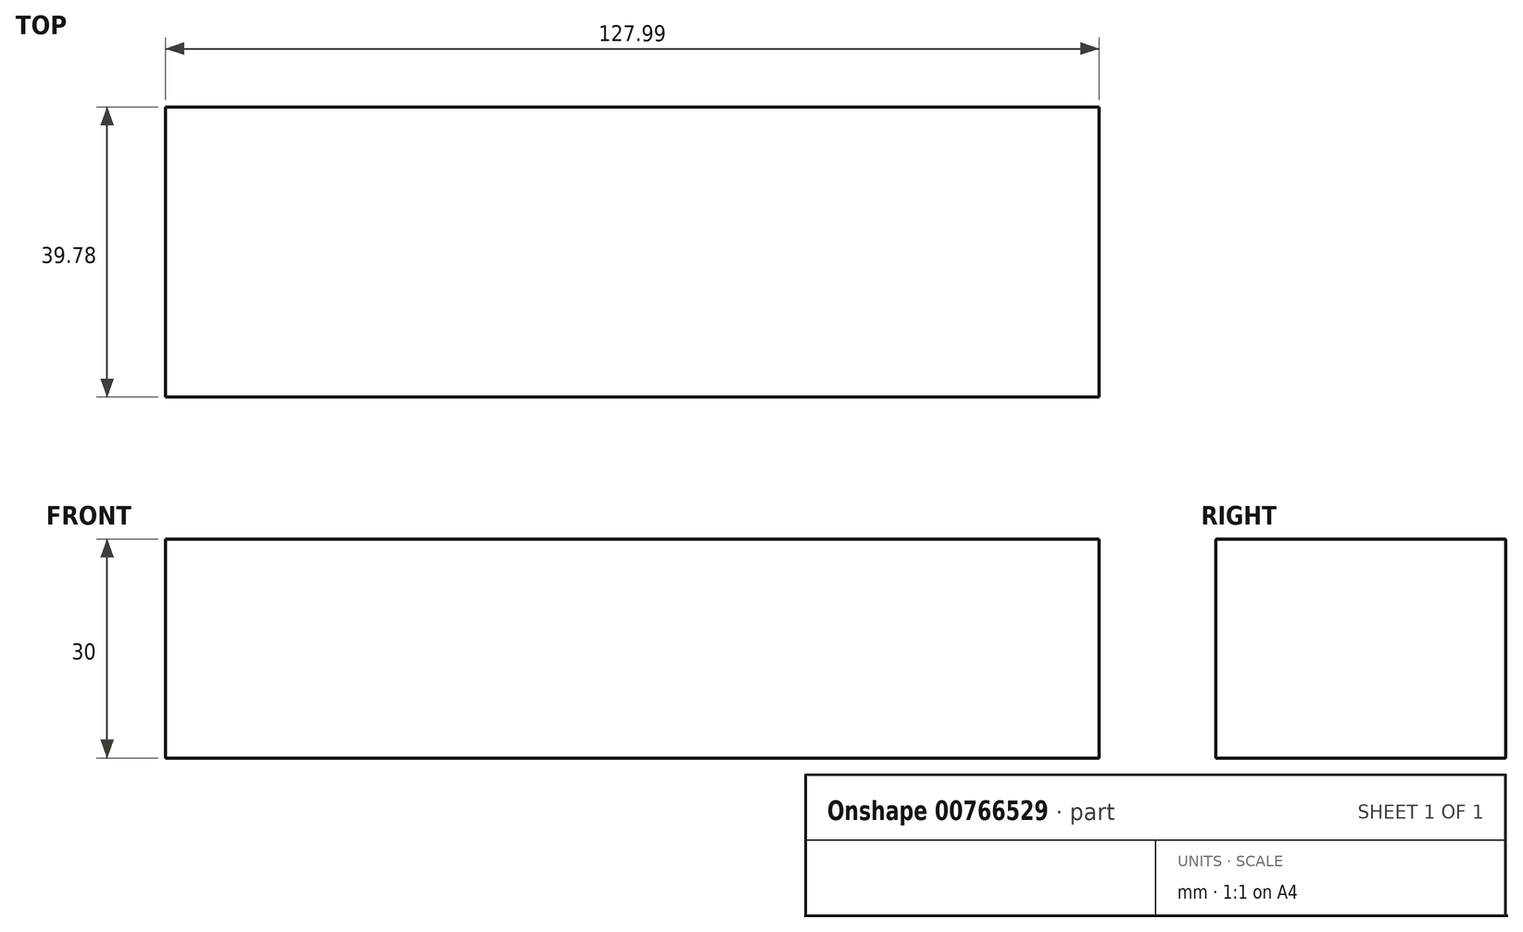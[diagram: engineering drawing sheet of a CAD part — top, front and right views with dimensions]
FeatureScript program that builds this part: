
annotation { "Feature Type Name" : "Feature", "Feature Type Description" : "" }
export const myFeature = defineFeature(function(context is Context, id is Id, definition is map)
    precondition{}
    {
        {
            var Q0;
            Q0=qCreatedBy(makeId("Top.planeOp"),FACE);
            var sketch = newSketch(context, id + "F0", { "sketchPlane" : qUnion([Q0])});
            skLineSegment(sketch, "E0.bottom", {"start": v(0, 0) * mm, "end": v(128, 0) * mm});
            skLineSegment(sketch, "E0.top", {"start": v(0, -39.78) * mm, "end": v(128, -39.78) * mm});
            skLineSegment(sketch, "E0.left", {"start": v(0, 0) * mm, "end": v(0, -39.78) * mm});
            skLineSegment(sketch, "E0.right", {"start": v(128, 0) * mm, "end": v(128, -39.78) * mm});
            skSolve(sketch);
        }
        {
            var Q0;
            Q0=makeQuery(id+"F0.imprint","IMPRINT",FACE,{"disambiguationData":[TD([[makeQuery(id+"F0.imprint","IMPRINT",EDGE,{"derivedFrom":sQuery(id+"F0.wireOp",EDGE,"E0.bottom")}),-1.0]])]});
            extrude(context, id + "F1", {"entities" : qUnion([Q0]), "depth" : 30 * mm, "offsetDistance" : 25.4 * mm});
        }
    });
